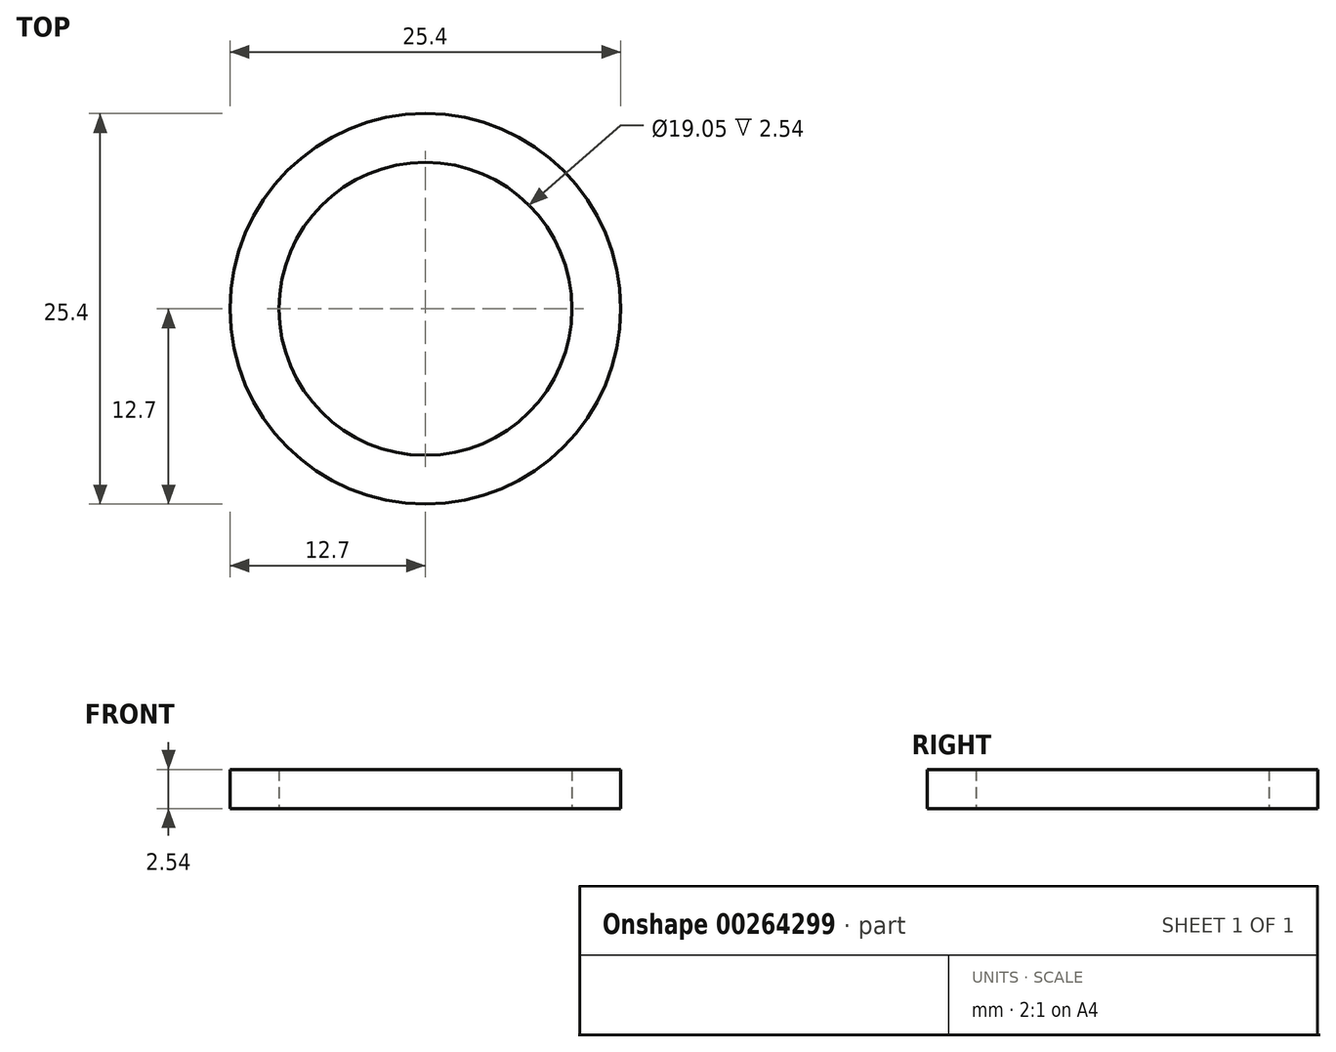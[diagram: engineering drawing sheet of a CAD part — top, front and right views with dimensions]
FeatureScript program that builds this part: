
annotation { "Feature Type Name" : "Feature", "Feature Type Description" : "" }
export const myFeature = defineFeature(function(context is Context, id is Id, definition is map)
    precondition{}
    {
        {
            var Q0;
            Q0=qCreatedBy(makeId("Top.planeOp"),FACE);
            var sketch = newSketch(context, id + "F0", { "sketchPlane" : qUnion([Q0])});
            skCircle(sketch, "E0", {"center": v(0, 0) * mm, "radius": 12.7 * mm});
            skCircle(sketch, "E1", {"center": v(0, 0) * mm, "radius": 9.53 * mm});
            skSolve(sketch);
        }
        {
            var Q0;
            Q0=makeQuery(id+"F0.imprint","IMPRINT",FACE,{"disambiguationData":[TD([[makeQuery(id+"F0.imprint","IMPRINT",EDGE,{"derivedFrom":sQuery(id+"F0.wireOp",EDGE,"E0")}),1.0]])]});
            extrude(context, id + "F1", {"entities" : qUnion([Q0]), "depth" : 2.54 * mm});
        }
    });
